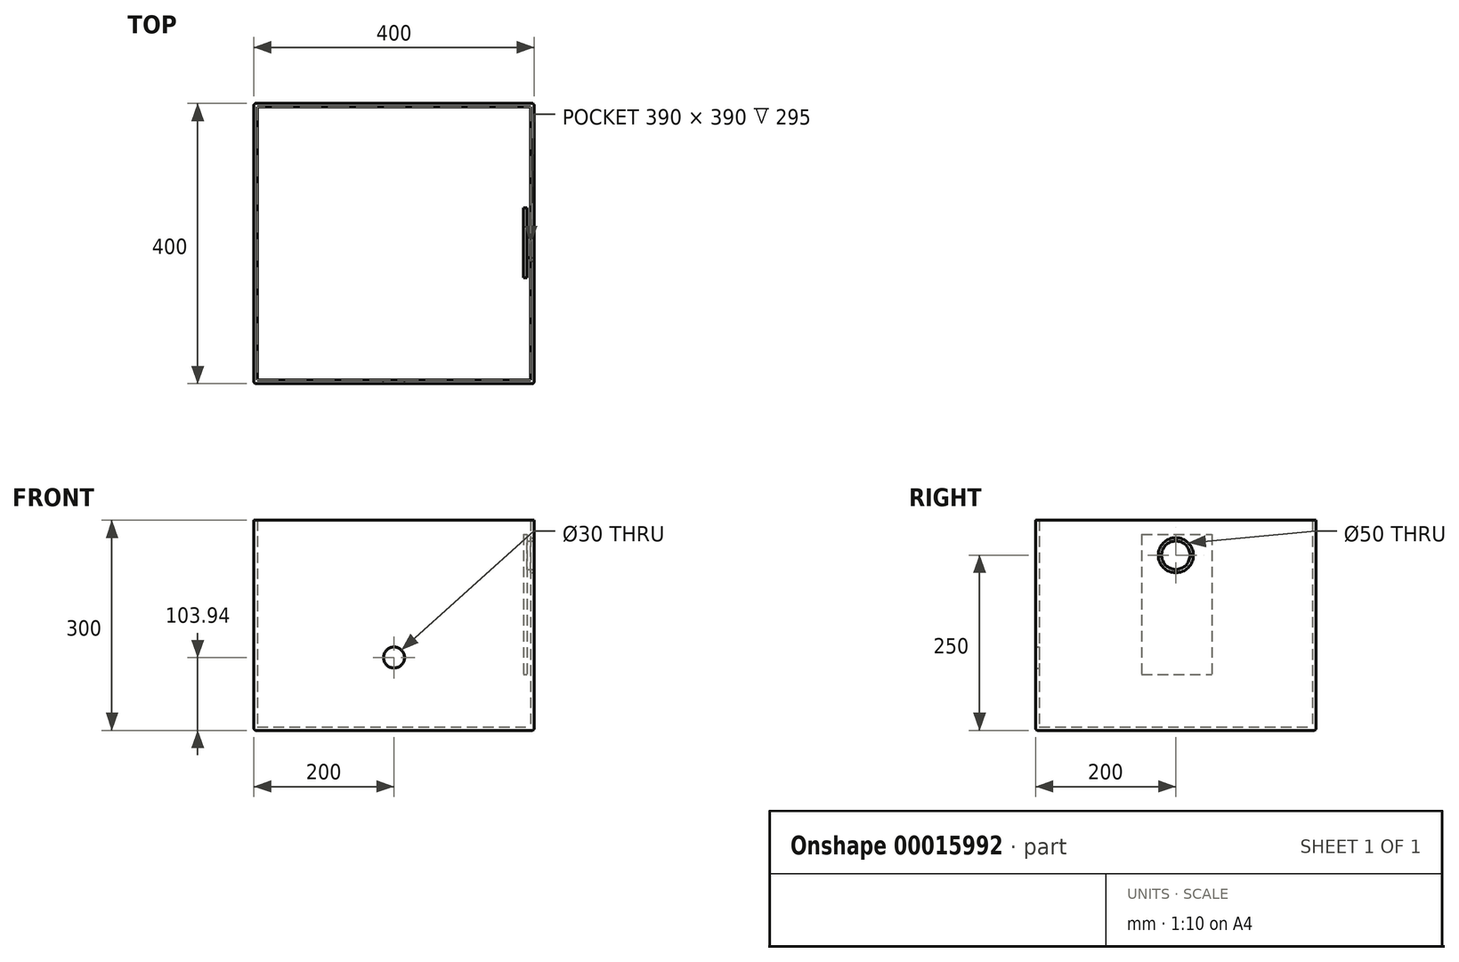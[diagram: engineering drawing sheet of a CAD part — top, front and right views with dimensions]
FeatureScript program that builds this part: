
annotation { "Feature Type Name" : "Feature", "Feature Type Description" : "" }
export const myFeature = defineFeature(function(context is Context, id is Id, definition is map)
    precondition{}
    {
        {
            var Q0;
            Q0=qCreatedBy(makeId("Front.planeOp"),FACE);
            var sketch = newSketch(context, id + "F0", { "sketchPlane" : qUnion([Q0])});
            skLineSegment(sketch, "E0", {"start": v(0, 0) * mm, "end": v(200, 0) * mm});
            skLineSegment(sketch, "E1", {"start": v(200, 0) * mm, "end": v(200, 300) * mm});
            skLineSegment(sketch, "E2", {"start": v(200, 300) * mm, "end": v(195, 300) * mm});
            skLineSegment(sketch, "E3", {"start": v(195, 300) * mm, "end": v(195, 5) * mm});
            skLineSegment(sketch, "E4", {"start": v(195, 5) * mm, "end": v(0, 5) * mm});
            skLineSegment(sketch, "E5", {"start": v(0, 5) * mm, "end": v(0, 0) * mm});
            skLineSegment(sketch, "E6.MirrorCS", {"start": v(-195, 300) * mm, "end": v(-195, 5) * mm});
            skLineSegment(sketch, "E7.MirrorCS", {"start": v(-200, 0) * mm, "end": v(-200, 300) * mm});
            skLineSegment(sketch, "E8.MirrorCS", {"start": v(-200, 300) * mm, "end": v(-195, 300) * mm});
            skLineSegment(sketch, "E9.MirrorCS", {"start": v(-195, 5) * mm, "end": v(0, 5) * mm});
            skLineSegment(sketch, "E10.MirrorCS", {"start": v(0, 0) * mm, "end": v(-200, 0) * mm});
            skSolve(sketch);
        }
        {
            var Q0;
            Q0 = qSketchRegion(id + "F0", true);
            extrude(context, id + "F1", {"entities" : qUnion([Q0]), "depth" : 200 * mm});
        }
        {
            var Q0;
            Q0=makeQuery(id+"F1.opExtrude","SWEPT_FACE",FACE,{"disambiguationData":[OSD([sQuery(id+"F0.wireOp",EDGE,"E4"),sQuery(id+"F0.wireOp",EDGE,"E9.MirrorCS")])]});
            var sketch = newSketch(context, id + "F2", { "sketchPlane" : qUnion([Q0])});
            skLineSegment(sketch, "E11.bottom", {"start": v(-195, -200) * mm, "end": v(195, -200) * mm});
            skLineSegment(sketch, "E11.top", {"start": v(-195, -195) * mm, "end": v(195, -195) * mm});
            skLineSegment(sketch, "E11.left", {"start": v(-195, -200) * mm, "end": v(-195, -195) * mm});
            skLineSegment(sketch, "E11.right", {"start": v(195, -200) * mm, "end": v(195, -195) * mm});
            skSolve(sketch);
        }
        {
            var Q0;
            Q0 = qSketchRegion(id + "F2", true);
            extrude(context, id + "F3", {"entities" : qUnion([Q0]), "operationType" : NewBodyOperationType.ADD, "depth" : 295 * mm});
        }
        {
            var Q0;
            Q0=makeQuery(id+"F1.opExtrude","SWEPT_BODY",BODY,{"disambiguationData":[OSD([sQuery(id+"F0.wireOp",EDGE,"E0"),sQuery(id+"F0.wireOp",EDGE,"E1"),sQuery(id+"F0.wireOp",EDGE,"E2"),sQuery(id+"F0.wireOp",EDGE,"E3"),sQuery(id+"F0.wireOp",EDGE,"E4"),sQuery(id+"F0.wireOp",EDGE,"E6.MirrorCS"),sQuery(id+"F0.wireOp",EDGE,"E7.MirrorCS"),sQuery(id+"F0.wireOp",EDGE,"E8.MirrorCS"),sQuery(id+"F0.wireOp",EDGE,"E9.MirrorCS"),sQuery(id+"F0.wireOp",EDGE,"E10.MirrorCS")])]});
            var Q1;
            Q1=qCreatedBy(makeId("Front.planeOp"),FACE);
            mirror(context, id + "F4", {"operationType" : NewBodyOperationType.ADD, "entities" : qUnion([Q0]), "mirrorPlane" : qUnion([Q1])});
        }
        {
            var Q0;
            {var subQ0=makeQuery(id+"F1.opExtrude","SWEPT_FACE",FACE,{"disambiguationData":[OSD([sQuery(id+"F0.wireOp",EDGE,"E7.MirrorCS")])]});Q0=makeQuery(id+"F4.boolean.opBoolean","MERGE",FACE,{"derivedFrom":[subQ0,makeQuery(id+"F4.opPattern","COPY",FACE,{"derivedFrom":subQ0,"instanceName":"1"})]});}
            var sketch = newSketch(context, id + "F5", { "sketchPlane" : qUnion([Q0])});
            skLineSegment(sketch, "E12.bottom", {"start": v(-200, 300) * mm, "end": v(200, 300) * mm});
            skLineSegment(sketch, "E12.top", {"start": v(-200, 320) * mm, "end": v(200, 320) * mm});
            skLineSegment(sketch, "E12.left", {"start": v(-200, 300) * mm, "end": v(-200, 320) * mm});
            skLineSegment(sketch, "E12.right", {"start": v(200, 300) * mm, "end": v(200, 320) * mm});
            skSolve(sketch);
        }
        {
            var Q0;
            Q0=makeQuery(id+"F4.opPattern","COPY",EDGE,{"derivedFrom":makeQuery(id+"F1.opExtrude","CAP_EDGE",EDGE,{"disambiguationData":[OSD([sQuery(id+"F0.wireOp",EDGE,"E1")])],"isStart":false}),"instanceName":"1"});
            var Q1;
            {var subQ0=makeQuery(id+"F1.opExtrude","SWEPT_EDGE",EDGE,{"disambiguationData":[OSD([sQuery(id+"F0.wireOp",EDGE,"E0"),sQuery(id+"F0.wireOp",EDGE,"E1")])]});Q1=makeQuery(id+"F4.boolean.opBoolean","MERGE",EDGE,{"derivedFrom":[subQ0,makeQuery(id+"F4.opPattern","COPY",EDGE,{"derivedFrom":subQ0,"instanceName":"1"})]});}
            var Q2;
            Q2=makeQuery(id+"F4.opPattern","COPY",EDGE,{"derivedFrom":makeQuery(id+"F1.opExtrude","CAP_EDGE",EDGE,{"disambiguationData":[OSD([sQuery(id+"F0.wireOp",EDGE,"E0"),sQuery(id+"F0.wireOp",EDGE,"E10.MirrorCS")])],"isStart":false}),"instanceName":"1"});
            var Q3;
            Q3=makeQuery(id+"F4.opPattern","COPY",EDGE,{"derivedFrom":makeQuery(id+"F1.opExtrude","CAP_EDGE",EDGE,{"disambiguationData":[OSD([sQuery(id+"F0.wireOp",EDGE,"E7.MirrorCS")])],"isStart":false}),"instanceName":"1"});
            var Q4;
            Q4=makeQuery(id+"F0aFheVfIjX7SRM_1.opExtrude","CAP_EDGE",EDGE,{"disambiguationData":[OSD([sQuery(id+"F5.wireOp",EDGE,"E12.left")])],"isStart":true});
            var Q5;
            Q5=makeQuery(id+"F0aFheVfIjX7SRM_1.opExtrude","CAP_EDGE",EDGE,{"disambiguationData":[OSD([sQuery(id+"F5.wireOp",EDGE,"E12.left")])],"isStart":false});
            var Q6;
            Q6=makeQuery(id+"F1.opExtrude","CAP_EDGE",EDGE,{"disambiguationData":[OSD([sQuery(id+"F0.wireOp",EDGE,"E1")])],"isStart":false});
            var Q7;
            Q7=makeQuery(id+"F0aFheVfIjX7SRM_1.opExtrude","CAP_EDGE",EDGE,{"disambiguationData":[OSD([sQuery(id+"F5.wireOp",EDGE,"E12.right")])],"isStart":false});
            var Q8;
            Q8=makeQuery(id+"F1.opExtrude","CAP_EDGE",EDGE,{"disambiguationData":[OSD([sQuery(id+"F0.wireOp",EDGE,"E7.MirrorCS")])],"isStart":false});
            var Q9;
            {var subQ0=makeQuery(id+"F1.opExtrude","SWEPT_EDGE",EDGE,{"disambiguationData":[OSD([sQuery(id+"F0.wireOp",EDGE,"E7.MirrorCS"),sQuery(id+"F0.wireOp",EDGE,"E10.MirrorCS")])]});Q9=makeQuery(id+"F4.boolean.opBoolean","MERGE",EDGE,{"derivedFrom":[subQ0,makeQuery(id+"F4.opPattern","COPY",EDGE,{"derivedFrom":subQ0,"instanceName":"1"})]});}
            var Q10;
            Q10=makeQuery(id+"F1.opExtrude","CAP_EDGE",EDGE,{"disambiguationData":[OSD([sQuery(id+"F0.wireOp",EDGE,"E0"),sQuery(id+"F0.wireOp",EDGE,"E10.MirrorCS")])],"isStart":false});
            var Q11;
            Q11=makeQuery(id+"F0aFheVfIjX7SRM_1.opExtrude","CAP_EDGE",EDGE,{"disambiguationData":[OSD([sQuery(id+"F5.wireOp",EDGE,"E12.right")])],"isStart":true});
            var Q12;
            Q12=makeQuery(id+"F0aFheVfIjX7SRM_1.opExtrude","SWEPT_FACE",FACE,{"disambiguationData":[OSD([sQuery(id+"F5.wireOp",EDGE,"E12.top")])]});
            fillet(context, id + "F6", {"entities" : qUnion([Q0, Q1, Q2, Q3, Q4, Q5, Q6, Q7, Q8, Q9, Q10, Q11, Q12]), "radius" : 3 * mm, "tangentPropagation" : true, "allowEdgeOverflow" : false});
        }
        {
            var Q0;
            Q0=makeQuery(id+"F3.opExtrude","SWEPT_FACE",FACE,{"disambiguationData":[OSD([sQuery(id+"F2.wireOp",EDGE,"E11.top")])]});
            var sketch = newSketch(context, id + "F7", { "sketchPlane" : qUnion([Q0])});
            skCircle(sketch, "E13", {"center": v(0, 103.94) * mm, "radius": 15 * mm});
            skSolve(sketch);
        }
        {
            var Q0;
            Q0 = qSketchRegion(id + "F7", true);
            var Q1;
            Q1=makeQuery(id+"F3.boolean.opBoolean","MERGE",FACE,{"derivedFrom":[makeQuery(id+"F1.opExtrude","CAP_FACE",FACE,{"disambiguationData":[OSD([sQuery(id+"F0.wireOp",EDGE,"E0"),sQuery(id+"F0.wireOp",EDGE,"E1"),sQuery(id+"F0.wireOp",EDGE,"E2"),sQuery(id+"F0.wireOp",EDGE,"E3"),sQuery(id+"F0.wireOp",EDGE,"E4"),sQuery(id+"F0.wireOp",EDGE,"E6.MirrorCS"),sQuery(id+"F0.wireOp",EDGE,"E7.MirrorCS"),sQuery(id+"F0.wireOp",EDGE,"E8.MirrorCS"),sQuery(id+"F0.wireOp",EDGE,"E9.MirrorCS"),sQuery(id+"F0.wireOp",EDGE,"E10.MirrorCS")])],"isStart":false}),makeQuery(id+"F3.opExtrude","SWEPT_FACE",FACE,{"disambiguationData":[OSD([sQuery(id+"F2.wireOp",EDGE,"E11.bottom")])]})]});
            extrude(context, id + "F8", {"entities" : qUnion([Q0]), "operationType" : NewBodyOperationType.REMOVE, "endBound" : BoundingType.UP_TO_SURFACE, "oppositeDirection" : true, "endBoundEntityFace" : qUnion([Q1]), "depth" : 25.4 * mm});
        }
        {
            var Q0;
            {var subQ0=makeQuery(id+"F1.opExtrude","SWEPT_FACE",FACE,{"disambiguationData":[OSD([sQuery(id+"F0.wireOp",EDGE,"E1")])]});Q0=makeQuery(id+"F4.boolean.opBoolean","MERGE",FACE,{"derivedFrom":[subQ0,makeQuery(id+"F4.opPattern","COPY",FACE,{"derivedFrom":subQ0,"instanceName":"1"})]});}
            var sketch = newSketch(context, id + "F9", { "sketchPlane" : qUnion([Q0])});
            skCircle(sketch, "E14", {"center": v(0, 250) * mm, "radius": 25 * mm});
            skSolve(sketch);
        }
        {
            var Q0;
            Q0 = qSketchRegion(id + "F9", true);
            extrude(context, id + "F10", {"entities" : qUnion([Q0]), "operationType" : NewBodyOperationType.REMOVE, "oppositeDirection" : true, "depth" : 25.4 * mm});
        }
        {
            var Q0;
            {var subQ0=makeQuery(id+"F1.opExtrude","SWEPT_FACE",FACE,{"disambiguationData":[OSD([sQuery(id+"F0.wireOp",EDGE,"E1")])]});Q0=makeQuery(id+"F4.boolean.opBoolean","MERGE",FACE,{"derivedFrom":[subQ0,makeQuery(id+"F4.opPattern","COPY",FACE,{"derivedFrom":subQ0,"instanceName":"1"})]});}
            var sketch = newSketch(context, id + "F11", { "sketchPlane" : qUnion([Q0])});
            skCircle(sketch, "E15", {"center": v(0, 250) * mm, "radius": 20.29 * mm});
            skSolve(sketch);
        }
        {
            var Q0;
            Q0 = qSketchRegion(id + "F11", true);
            extrude(context, id + "F12", {"entities" : qUnion([Q0]), "oppositeDirection" : true, "depth" : 10 * mm});
        }
        {
            var Q0;
            Q0=makeQuery(id+"F12.opExtrude","CAP_FACE",FACE,{"disambiguationData":[OSD([sQuery(id+"F11.wireOp",EDGE,"E15")])],"isStart":false});
            var sketch = newSketch(context, id + "F13", { "sketchPlane" : qUnion([Q0])});
            skLineSegment(sketch, "E16.bottom", {"start": v(48.84, 279.71) * mm, "end": v(-51.16, 279.71) * mm});
            skLineSegment(sketch, "E16.top", {"start": v(48.84, 79.71) * mm, "end": v(-51.16, 79.71) * mm});
            skLineSegment(sketch, "E16.left", {"start": v(48.84, 279.71) * mm, "end": v(48.84, 79.71) * mm});
            skLineSegment(sketch, "E16.right", {"start": v(-51.16, 279.71) * mm, "end": v(-51.16, 79.71) * mm});
            skSolve(sketch);
        }
        {
            var Q0;
            Q0 = qSketchRegion(id + "F13", true);
            extrude(context, id + "F14", {"entities" : qUnion([Q0]), "operationType" : NewBodyOperationType.ADD, "depth" : 5 * mm});
        }
        {
            var Q0;
            Q0=makeQuery(id+"F14.opExtrude","SWEPT_FACE",FACE,{"disambiguationData":[OSD([sQuery(id+"F13.wireOp",EDGE,"E16.bottom")])]});
            var sketch = newSketch(context, id + "F15", { "sketchPlane" : qUnion([Q0])});
            skLineSegment(sketch, "E17", {"start": v(185, 51.16) * mm, "end": v(170, 51.16) * mm});
            skLineSegment(sketch, "E18", {"start": v(170, 51.16) * mm, "end": v(170, 50.16) * mm});
            skLineSegment(sketch, "E19", {"start": v(170, 50.16) * mm, "end": v(180, 50.16) * mm});
            skLineSegment(sketch, "E20", {"start": v(180, 50.16) * mm, "end": v(180, 48.16) * mm});
            skLineSegment(sketch, "E21", {"start": v(180, 48.16) * mm, "end": v(170, 48.16) * mm});
            skLineSegment(sketch, "E22.1.0.0", {"start": v(170, 48.16) * mm, "end": v(170, 47.16) * mm});
            skLineSegment(sketch, "E22.1.0.1", {"start": v(170, 47.16) * mm, "end": v(180, 47.16) * mm});
            skLineSegment(sketch, "E22.1.0.2", {"start": v(180, 47.16) * mm, "end": v(180, 45.16) * mm});
            skLineSegment(sketch, "E22.1.0.3", {"start": v(180, 45.16) * mm, "end": v(170, 45.16) * mm});
            skLineSegment(sketch, "E22.2.0.0", {"start": v(169.99, 45.16) * mm, "end": v(169.99, 44.16) * mm});
            skLineSegment(sketch, "E22.2.0.1", {"start": v(169.99, 44.16) * mm, "end": v(179.99, 44.16) * mm});
            skLineSegment(sketch, "E22.2.0.2", {"start": v(179.99, 44.16) * mm, "end": v(179.99, 42.16) * mm});
            skLineSegment(sketch, "E22.2.0.3", {"start": v(179.99, 42.16) * mm, "end": v(169.99, 42.16) * mm});
            skLineSegment(sketch, "E22.3.0.0", {"start": v(169.98, 42.16) * mm, "end": v(169.98, 41.16) * mm});
            skLineSegment(sketch, "E22.3.0.1", {"start": v(169.98, 41.16) * mm, "end": v(179.98, 41.16) * mm});
            skLineSegment(sketch, "E22.3.0.2", {"start": v(179.98, 41.16) * mm, "end": v(179.98, 39.16) * mm});
            skLineSegment(sketch, "E22.3.0.3", {"start": v(179.98, 39.16) * mm, "end": v(169.98, 39.16) * mm});
            skLineSegment(sketch, "E22.4.0.0", {"start": v(169.97, 39.16) * mm, "end": v(169.97, 38.16) * mm});
            skLineSegment(sketch, "E22.4.0.1", {"start": v(169.97, 38.16) * mm, "end": v(179.97, 38.16) * mm});
            skLineSegment(sketch, "E22.4.0.2", {"start": v(179.97, 38.16) * mm, "end": v(179.97, 36.16) * mm});
            skLineSegment(sketch, "E22.4.0.3", {"start": v(179.97, 36.16) * mm, "end": v(169.97, 36.16) * mm});
            skLineSegment(sketch, "E22.5.0.0", {"start": v(169.97, 36.16) * mm, "end": v(169.97, 35.16) * mm});
            skLineSegment(sketch, "E22.5.0.1", {"start": v(169.97, 35.16) * mm, "end": v(179.97, 35.16) * mm});
            skLineSegment(sketch, "E22.5.0.2", {"start": v(179.97, 35.16) * mm, "end": v(179.97, 33.16) * mm});
            skLineSegment(sketch, "E22.5.0.3", {"start": v(179.97, 33.16) * mm, "end": v(169.97, 33.16) * mm});
            skLineSegment(sketch, "E22.6.0.0", {"start": v(169.96, 33.16) * mm, "end": v(169.96, 32.16) * mm});
            skLineSegment(sketch, "E22.6.0.1", {"start": v(169.96, 32.16) * mm, "end": v(179.96, 32.16) * mm});
            skLineSegment(sketch, "E22.6.0.2", {"start": v(179.96, 32.16) * mm, "end": v(179.96, 30.16) * mm});
            skLineSegment(sketch, "E22.6.0.3", {"start": v(179.96, 30.16) * mm, "end": v(169.96, 30.16) * mm});
            skLineSegment(sketch, "E22.7.0.0", {"start": v(169.95, 30.16) * mm, "end": v(169.95, 29.16) * mm});
            skLineSegment(sketch, "E22.7.0.1", {"start": v(169.95, 29.16) * mm, "end": v(179.95, 29.16) * mm});
            skLineSegment(sketch, "E22.7.0.2", {"start": v(179.95, 29.16) * mm, "end": v(179.95, 27.16) * mm});
            skLineSegment(sketch, "E22.7.0.3", {"start": v(179.95, 27.16) * mm, "end": v(169.95, 27.16) * mm});
            skLineSegment(sketch, "E22.8.0.0", {"start": v(169.95, 27.16) * mm, "end": v(169.95, 26.16) * mm});
            skLineSegment(sketch, "E22.8.0.1", {"start": v(169.95, 26.16) * mm, "end": v(179.95, 26.16) * mm});
            skLineSegment(sketch, "E22.8.0.2", {"start": v(179.95, 26.16) * mm, "end": v(179.95, 24.16) * mm});
            skLineSegment(sketch, "E22.8.0.3", {"start": v(179.95, 24.16) * mm, "end": v(169.95, 24.16) * mm});
            skLineSegment(sketch, "E22.9.0.0", {"start": v(169.94, 24.16) * mm, "end": v(169.94, 23.16) * mm});
            skLineSegment(sketch, "E22.9.0.1", {"start": v(169.94, 23.16) * mm, "end": v(179.94, 23.16) * mm});
            skLineSegment(sketch, "E22.9.0.2", {"start": v(179.94, 23.16) * mm, "end": v(179.94, 21.16) * mm});
            skLineSegment(sketch, "E22.9.0.3", {"start": v(179.94, 21.16) * mm, "end": v(169.94, 21.16) * mm});
            skLineSegment(sketch, "E22.10.0.0", {"start": v(169.93, 21.16) * mm, "end": v(169.93, 20.16) * mm});
            skLineSegment(sketch, "E22.10.0.1", {"start": v(169.93, 20.16) * mm, "end": v(179.93, 20.16) * mm});
            skLineSegment(sketch, "E22.10.0.2", {"start": v(179.93, 20.16) * mm, "end": v(179.93, 18.16) * mm});
            skLineSegment(sketch, "E22.10.0.3", {"start": v(179.93, 18.16) * mm, "end": v(169.93, 18.16) * mm});
            skLineSegment(sketch, "E22.11.0.0", {"start": v(169.93, 18.16) * mm, "end": v(169.93, 17.16) * mm});
            skLineSegment(sketch, "E22.11.0.1", {"start": v(169.93, 17.16) * mm, "end": v(179.93, 17.16) * mm});
            skLineSegment(sketch, "E22.11.0.2", {"start": v(179.93, 17.16) * mm, "end": v(179.93, 15.16) * mm});
            skLineSegment(sketch, "E22.11.0.3", {"start": v(179.93, 15.16) * mm, "end": v(169.93, 15.16) * mm});
            skLineSegment(sketch, "E22.12.0.0", {"start": v(169.92, 15.16) * mm, "end": v(169.92, 14.16) * mm});
            skLineSegment(sketch, "E22.12.0.1", {"start": v(169.92, 14.16) * mm, "end": v(179.92, 14.16) * mm});
            skLineSegment(sketch, "E22.12.0.2", {"start": v(179.92, 14.16) * mm, "end": v(179.92, 12.16) * mm});
            skLineSegment(sketch, "E22.12.0.3", {"start": v(179.92, 12.16) * mm, "end": v(169.92, 12.16) * mm});
            skLineSegment(sketch, "E22.13.0.0", {"start": v(169.91, 12.16) * mm, "end": v(169.91, 11.16) * mm});
            skLineSegment(sketch, "E22.13.0.1", {"start": v(169.91, 11.16) * mm, "end": v(179.91, 11.16) * mm});
            skLineSegment(sketch, "E22.13.0.2", {"start": v(179.91, 11.16) * mm, "end": v(179.91, 9.16) * mm});
            skLineSegment(sketch, "E22.13.0.3", {"start": v(179.91, 9.16) * mm, "end": v(169.91, 9.16) * mm});
            skLineSegment(sketch, "E22.14.0.0", {"start": v(169.9, 9.16) * mm, "end": v(169.9, 8.16) * mm});
            skLineSegment(sketch, "E22.14.0.1", {"start": v(169.9, 8.16) * mm, "end": v(179.9, 8.16) * mm});
            skLineSegment(sketch, "E22.14.0.2", {"start": v(179.9, 8.16) * mm, "end": v(179.9, 6.16) * mm});
            skLineSegment(sketch, "E22.14.0.3", {"start": v(179.9, 6.16) * mm, "end": v(169.9, 6.16) * mm});
            skLineSegment(sketch, "E22.15.0.0", {"start": v(169.9, 6.16) * mm, "end": v(169.9, 5.16) * mm});
            skLineSegment(sketch, "E22.15.0.1", {"start": v(169.9, 5.16) * mm, "end": v(179.9, 5.16) * mm});
            skLineSegment(sketch, "E22.15.0.2", {"start": v(179.9, 5.16) * mm, "end": v(179.9, 3.16) * mm});
            skLineSegment(sketch, "E22.15.0.3", {"start": v(179.9, 3.16) * mm, "end": v(169.9, 3.16) * mm});
            skLineSegment(sketch, "E22.16.0.0", {"start": v(169.9, 3.16) * mm, "end": v(169.9, 2.16) * mm});
            skLineSegment(sketch, "E22.16.0.1", {"start": v(169.9, 2.16) * mm, "end": v(179.9, 2.16) * mm});
            skLineSegment(sketch, "E22.16.0.2", {"start": v(179.9, 2.16) * mm, "end": v(179.9, 0.16) * mm});
            skLineSegment(sketch, "E22.16.0.3", {"start": v(179.9, 0.16) * mm, "end": v(169.9, 0.16) * mm});
            skLineSegment(sketch, "E22.17.0.0", {"start": v(169.89, 0.16) * mm, "end": v(169.89, -0.84) * mm});
            skLineSegment(sketch, "E22.17.0.1", {"start": v(169.89, -0.84) * mm, "end": v(179.89, -0.84) * mm});
            skLineSegment(sketch, "E22.17.0.2", {"start": v(179.89, -0.84) * mm, "end": v(179.89, -2.84) * mm});
            skLineSegment(sketch, "E22.17.0.3", {"start": v(179.89, -2.84) * mm, "end": v(169.89, -2.84) * mm});
            skLineSegment(sketch, "E22.18.0.0", {"start": v(169.88, -2.84) * mm, "end": v(169.88, -3.84) * mm});
            skLineSegment(sketch, "E22.18.0.1", {"start": v(169.88, -3.84) * mm, "end": v(179.88, -3.84) * mm});
            skLineSegment(sketch, "E22.18.0.2", {"start": v(179.88, -3.84) * mm, "end": v(179.88, -5.84) * mm});
            skLineSegment(sketch, "E22.18.0.3", {"start": v(179.88, -5.84) * mm, "end": v(169.88, -5.84) * mm});
            skLineSegment(sketch, "E22.19.0.0", {"start": v(169.87, -5.84) * mm, "end": v(169.87, -6.84) * mm});
            skLineSegment(sketch, "E22.19.0.1", {"start": v(169.87, -6.84) * mm, "end": v(179.87, -6.84) * mm});
            skLineSegment(sketch, "E22.19.0.2", {"start": v(179.87, -6.84) * mm, "end": v(179.87, -8.84) * mm});
            skLineSegment(sketch, "E22.19.0.3", {"start": v(179.87, -8.84) * mm, "end": v(169.87, -8.84) * mm});
            skLineSegment(sketch, "E22.20.0.0", {"start": v(169.87, -8.84) * mm, "end": v(169.87, -9.84) * mm});
            skLineSegment(sketch, "E22.20.0.1", {"start": v(169.87, -9.84) * mm, "end": v(179.87, -9.84) * mm});
            skLineSegment(sketch, "E22.20.0.2", {"start": v(179.87, -9.84) * mm, "end": v(179.87, -11.84) * mm});
            skLineSegment(sketch, "E22.20.0.3", {"start": v(179.87, -11.84) * mm, "end": v(169.87, -11.84) * mm});
            skLineSegment(sketch, "E22.21.0.0", {"start": v(169.86, -11.84) * mm, "end": v(169.86, -12.84) * mm});
            skLineSegment(sketch, "E22.21.0.1", {"start": v(169.86, -12.84) * mm, "end": v(179.86, -12.84) * mm});
            skLineSegment(sketch, "E22.21.0.2", {"start": v(179.86, -12.84) * mm, "end": v(179.86, -14.84) * mm});
            skLineSegment(sketch, "E22.21.0.3", {"start": v(179.86, -14.84) * mm, "end": v(169.86, -14.84) * mm});
            skLineSegment(sketch, "E22.22.0.0", {"start": v(169.85, -14.84) * mm, "end": v(169.85, -15.84) * mm});
            skLineSegment(sketch, "E22.22.0.1", {"start": v(169.85, -15.84) * mm, "end": v(179.85, -15.84) * mm});
            skLineSegment(sketch, "E22.22.0.2", {"start": v(179.85, -15.84) * mm, "end": v(179.85, -17.84) * mm});
            skLineSegment(sketch, "E22.22.0.3", {"start": v(179.85, -17.84) * mm, "end": v(169.85, -17.84) * mm});
            skLineSegment(sketch, "E22.23.0.0", {"start": v(169.85, -17.84) * mm, "end": v(169.85, -18.84) * mm});
            skLineSegment(sketch, "E22.23.0.1", {"start": v(169.85, -18.84) * mm, "end": v(179.85, -18.84) * mm});
            skLineSegment(sketch, "E22.23.0.2", {"start": v(179.85, -18.84) * mm, "end": v(179.85, -20.84) * mm});
            skLineSegment(sketch, "E22.23.0.3", {"start": v(179.85, -20.84) * mm, "end": v(169.85, -20.84) * mm});
            skLineSegment(sketch, "E22.24.0.0", {"start": v(169.84, -20.84) * mm, "end": v(169.84, -21.84) * mm});
            skLineSegment(sketch, "E22.24.0.1", {"start": v(169.84, -21.84) * mm, "end": v(179.84, -21.84) * mm});
            skLineSegment(sketch, "E22.24.0.2", {"start": v(179.84, -21.84) * mm, "end": v(179.84, -23.84) * mm});
            skLineSegment(sketch, "E22.24.0.3", {"start": v(179.84, -23.84) * mm, "end": v(169.84, -23.84) * mm});
            skLineSegment(sketch, "E22.25.0.0", {"start": v(169.83, -23.84) * mm, "end": v(169.83, -24.84) * mm});
            skLineSegment(sketch, "E22.25.0.1", {"start": v(169.83, -24.84) * mm, "end": v(179.83, -24.84) * mm});
            skLineSegment(sketch, "E22.25.0.2", {"start": v(179.83, -24.84) * mm, "end": v(179.83, -26.84) * mm});
            skLineSegment(sketch, "E22.25.0.3", {"start": v(179.83, -26.84) * mm, "end": v(169.83, -26.84) * mm});
            skLineSegment(sketch, "E22.26.0.0", {"start": v(169.83, -26.84) * mm, "end": v(169.83, -27.84) * mm});
            skLineSegment(sketch, "E22.26.0.1", {"start": v(169.83, -27.84) * mm, "end": v(179.83, -27.84) * mm});
            skLineSegment(sketch, "E22.26.0.2", {"start": v(179.83, -27.84) * mm, "end": v(179.83, -29.84) * mm});
            skLineSegment(sketch, "E22.26.0.3", {"start": v(179.83, -29.84) * mm, "end": v(169.83, -29.84) * mm});
            skLineSegment(sketch, "E22.27.0.0", {"start": v(169.82, -29.84) * mm, "end": v(169.82, -30.84) * mm});
            skLineSegment(sketch, "E22.27.0.1", {"start": v(169.82, -30.84) * mm, "end": v(179.82, -30.84) * mm});
            skLineSegment(sketch, "E22.27.0.2", {"start": v(179.82, -30.84) * mm, "end": v(179.82, -32.84) * mm});
            skLineSegment(sketch, "E22.27.0.3", {"start": v(179.82, -32.84) * mm, "end": v(169.82, -32.84) * mm});
            skLineSegment(sketch, "E22.28.0.0", {"start": v(169.81, -32.84) * mm, "end": v(169.81, -33.84) * mm});
            skLineSegment(sketch, "E22.28.0.1", {"start": v(169.81, -33.84) * mm, "end": v(179.81, -33.84) * mm});
            skLineSegment(sketch, "E22.28.0.2", {"start": v(179.81, -33.84) * mm, "end": v(179.81, -35.84) * mm});
            skLineSegment(sketch, "E22.28.0.3", {"start": v(179.81, -35.84) * mm, "end": v(169.81, -35.84) * mm});
            skLineSegment(sketch, "E22.29.0.0", {"start": v(169.8, -35.84) * mm, "end": v(169.8, -36.84) * mm});
            skLineSegment(sketch, "E22.29.0.1", {"start": v(169.8, -36.84) * mm, "end": v(179.8, -36.84) * mm});
            skLineSegment(sketch, "E22.29.0.2", {"start": v(179.8, -36.84) * mm, "end": v(179.8, -38.84) * mm});
            skLineSegment(sketch, "E22.29.0.3", {"start": v(179.8, -38.84) * mm, "end": v(169.8, -38.84) * mm});
            skLineSegment(sketch, "E22.30.0.0", {"start": v(169.8, -38.84) * mm, "end": v(169.8, -39.84) * mm});
            skLineSegment(sketch, "E22.30.0.1", {"start": v(169.8, -39.84) * mm, "end": v(179.8, -39.84) * mm});
            skLineSegment(sketch, "E22.30.0.2", {"start": v(179.8, -39.84) * mm, "end": v(179.8, -41.84) * mm});
            skLineSegment(sketch, "E22.30.0.3", {"start": v(179.8, -41.84) * mm, "end": v(169.8, -41.84) * mm});
            skLineSegment(sketch, "E22.31.0.0", {"start": v(169.8, -41.84) * mm, "end": v(169.8, -42.84) * mm});
            skLineSegment(sketch, "E22.31.0.1", {"start": v(169.8, -42.84) * mm, "end": v(179.8, -42.84) * mm});
            skLineSegment(sketch, "E22.31.0.2", {"start": v(179.8, -42.84) * mm, "end": v(179.8, -44.84) * mm});
            skLineSegment(sketch, "E22.31.0.3", {"start": v(179.8, -44.84) * mm, "end": v(169.8, -44.84) * mm});
            skLineSegment(sketch, "E22.32.0.0", {"start": v(169.79, -44.84) * mm, "end": v(169.79, -45.84) * mm});
            skLineSegment(sketch, "E22.32.0.1", {"start": v(169.79, -45.84) * mm, "end": v(179.79, -45.84) * mm});
            skLineSegment(sketch, "E22.32.0.2", {"start": v(179.79, -45.84) * mm, "end": v(179.79, -47.84) * mm});
            skLineSegment(sketch, "E22.32.0.3", {"start": v(179.79, -47.84) * mm, "end": v(169.79, -47.84) * mm});
            skLineSegment(sketch, "E22.33.0.0", {"start": v(169.78, -47.84) * mm, "end": v(169.78, -48.84) * mm});
            skLineSegment(sketch, "E22.33.0.1", {"start": v(169.78, -48.84) * mm, "end": v(185, -48.84) * mm});
            skLineSegment(sketch, "E23", {"start": v(185, 51.16) * mm, "end": v(185, -48.84) * mm});
            skSolve(sketch);
        }
        {
            var Q0;
            Q0=sQuery(id+"F15.wireOp",EDGE,"E22.18.0.3");
            var Q1;
            Q1=sQuery(id+"F15.wireOp",EDGE,"E22.14.0.3");
            var Q2;
            Q2=sQuery(id+"F15.wireOp",EDGE,"E22.10.0.3");
            var Q3;
            Q3=sQuery(id+"F15.wireOp",EDGE,"E22.6.0.3");
            var Q4;
            Q4=sQuery(id+"F15.wireOp",EDGE,"E22.30.0.3");
            var Q5;
            Q5=sQuery(id+"F15.wireOp",EDGE,"E22.26.0.3");
            var Q6;
            Q6=sQuery(id+"F15.wireOp",EDGE,"E22.22.0.3");
            var Q7;
            Q7=sQuery(id+"F15.wireOp",EDGE,"E22.3.0.1");
            var Q8;
            Q8=sQuery(id+"F15.wireOp",EDGE,"E19");
            var Q9;
            Q9=sQuery(id+"F15.wireOp",EDGE,"E21");
            var Q10;
            Q10=sQuery(id+"F15.wireOp",EDGE,"E22.1.0.1");
            var Q11;
            Q11=sQuery(id+"F15.wireOp",EDGE,"E22.1.0.3");
            var Q12;
            Q12=sQuery(id+"F15.wireOp",EDGE,"E22.2.0.1");
            var Q13;
            Q13=sQuery(id+"F15.wireOp",EDGE,"E22.2.0.3");
            var Q14;
            Q14=sQuery(id+"F15.wireOp",EDGE,"E22.7.0.1");
            var Q15;
            Q15=sQuery(id+"F15.wireOp",EDGE,"E22.23.0.1");
            var Q16;
            Q16=sQuery(id+"F15.wireOp",EDGE,"E22.19.0.1");
            var Q17;
            Q17=sQuery(id+"F15.wireOp",EDGE,"E22.15.0.1");
            var Q18;
            Q18=sQuery(id+"F15.wireOp",EDGE,"E22.11.0.1");
            var Q19;
            Q19=sQuery(id+"F15.wireOp",EDGE,"E22.31.0.1");
            var Q20;
            Q20=sQuery(id+"F15.wireOp",EDGE,"E22.27.0.1");
            var Q21;
            Q21=sQuery(id+"F15.wireOp",EDGE,"E22.7.0.3");
            var Q22;
            Q22=sQuery(id+"F15.wireOp",EDGE,"E22.3.0.3");
            var Q23;
            Q23=sQuery(id+"F15.wireOp",EDGE,"E22.23.0.3");
            var Q24;
            Q24=sQuery(id+"F15.wireOp",EDGE,"E22.19.0.3");
            var Q25;
            Q25=sQuery(id+"F15.wireOp",EDGE,"E22.15.0.3");
            var Q26;
            Q26=sQuery(id+"F15.wireOp",EDGE,"E22.11.0.3");
            var Q27;
            Q27=sQuery(id+"F15.wireOp",EDGE,"E22.31.0.3");
            var Q28;
            Q28=sQuery(id+"F15.wireOp",EDGE,"E22.27.0.3");
            var Q29;
            Q29=sQuery(id+"F15.wireOp",EDGE,"E22.8.0.1");
            var Q30;
            Q30=sQuery(id+"F15.wireOp",EDGE,"E22.4.0.1");
            var Q31;
            Q31=sQuery(id+"F15.wireOp",EDGE,"E22.24.0.1");
            var Q32;
            Q32=sQuery(id+"F15.wireOp",EDGE,"E22.20.0.1");
            var Q33;
            Q33=sQuery(id+"F15.wireOp",EDGE,"E22.16.0.1");
            var Q34;
            Q34=sQuery(id+"F15.wireOp",EDGE,"E22.12.0.1");
            var Q35;
            Q35=sQuery(id+"F15.wireOp",EDGE,"E22.32.0.1");
            var Q36;
            Q36=sQuery(id+"F15.wireOp",EDGE,"E22.28.0.1");
            var Q37;
            Q37=sQuery(id+"F15.wireOp",EDGE,"E22.8.0.3");
            var Q38;
            Q38=sQuery(id+"F15.wireOp",EDGE,"E22.4.0.3");
            var Q39;
            Q39=sQuery(id+"F15.wireOp",EDGE,"E22.24.0.3");
            var Q40;
            Q40=sQuery(id+"F15.wireOp",EDGE,"E22.20.0.3");
            var Q41;
            Q41=sQuery(id+"F15.wireOp",EDGE,"E22.16.0.3");
            var Q42;
            Q42=sQuery(id+"F15.wireOp",EDGE,"E22.12.0.3");
            var Q43;
            Q43=sQuery(id+"F15.wireOp",EDGE,"E22.32.0.3");
            var Q44;
            Q44=sQuery(id+"F15.wireOp",EDGE,"E22.28.0.3");
            var Q45;
            Q45=sQuery(id+"F15.wireOp",EDGE,"E22.9.0.1");
            var Q46;
            Q46=sQuery(id+"F15.wireOp",EDGE,"E22.5.0.1");
            var Q47;
            Q47=sQuery(id+"F15.wireOp",EDGE,"E22.25.0.1");
            var Q48;
            Q48=sQuery(id+"F15.wireOp",EDGE,"E22.21.0.1");
            var Q49;
            Q49=sQuery(id+"F15.wireOp",EDGE,"E22.17.0.1");
            var Q50;
            Q50=sQuery(id+"F15.wireOp",EDGE,"E22.13.0.1");
            var Q51;
            Q51=sQuery(id+"F15.wireOp",EDGE,"E22.29.0.1");
            var Q52;
            Q52=sQuery(id+"F15.wireOp",EDGE,"E22.17.0.3");
            var Q53;
            Q53=sQuery(id+"F15.wireOp",EDGE,"E22.13.0.3");
            var Q54;
            Q54=sQuery(id+"F15.wireOp",EDGE,"E22.9.0.3");
            var Q55;
            Q55=sQuery(id+"F15.wireOp",EDGE,"E22.5.0.3");
            var Q56;
            Q56=sQuery(id+"F15.wireOp",EDGE,"E22.29.0.3");
            var Q57;
            Q57=sQuery(id+"F15.wireOp",EDGE,"E22.25.0.3");
            var Q58;
            Q58=sQuery(id+"F15.wireOp",EDGE,"E22.21.0.3");
            var Q59;
            Q59=sQuery(id+"F15.wireOp",EDGE,"E22.18.0.1");
            var Q60;
            Q60=sQuery(id+"F15.wireOp",EDGE,"E22.14.0.1");
            var Q61;
            Q61=sQuery(id+"F15.wireOp",EDGE,"E22.10.0.1");
            var Q62;
            Q62=sQuery(id+"F15.wireOp",EDGE,"E22.6.0.1");
            var Q63;
            Q63=sQuery(id+"F15.wireOp",EDGE,"E22.30.0.1");
            var Q64;
            Q64=sQuery(id+"F15.wireOp",EDGE,"E22.26.0.1");
            var Q65;
            Q65=sQuery(id+"F15.wireOp",EDGE,"E22.22.0.1");
            var Q66;
            Q66=sQuery(id+"F15.wireOp",EDGE,"E22.18.0.2");
            var Q67;
            Q67=sQuery(id+"F15.wireOp",EDGE,"E22.14.0.2");
            var Q68;
            Q68=sQuery(id+"F15.wireOp",EDGE,"E22.10.0.2");
            var Q69;
            Q69=sQuery(id+"F15.wireOp",EDGE,"E22.6.0.2");
            var Q70;
            Q70=sQuery(id+"F15.wireOp",EDGE,"E22.30.0.2");
            var Q71;
            Q71=sQuery(id+"F15.wireOp",EDGE,"E22.26.0.2");
            var Q72;
            Q72=sQuery(id+"F15.wireOp",EDGE,"E22.3.0.2");
            var Q73;
            Q73=sQuery(id+"F15.wireOp",EDGE,"E18");
            var Q74;
            Q74=sQuery(id+"F15.wireOp",EDGE,"E20");
            var Q75;
            Q75=sQuery(id+"F15.wireOp",EDGE,"E22.1.0.0");
            var Q76;
            Q76=sQuery(id+"F15.wireOp",EDGE,"E22.1.0.2");
            var Q77;
            Q77=sQuery(id+"F15.wireOp",EDGE,"E22.2.0.0");
            var Q78;
            Q78=sQuery(id+"F15.wireOp",EDGE,"E22.19.0.0");
            var Q79;
            Q79=sQuery(id+"F15.wireOp",EDGE,"E22.7.0.2");
            var Q80;
            Q80=sQuery(id+"F15.wireOp",EDGE,"E22.23.0.2");
            var Q81;
            Q81=sQuery(id+"F15.wireOp",EDGE,"E22.19.0.2");
            var Q82;
            Q82=sQuery(id+"F15.wireOp",EDGE,"E22.15.0.2");
            var Q83;
            Q83=sQuery(id+"F15.wireOp",EDGE,"E22.11.0.2");
            var Q84;
            Q84=sQuery(id+"F15.wireOp",EDGE,"E22.31.0.2");
            var Q85;
            Q85=sQuery(id+"F15.wireOp",EDGE,"E22.27.0.2");
            var Q86;
            Q86=sQuery(id+"F15.wireOp",EDGE,"E22.8.0.0");
            var Q87;
            Q87=sQuery(id+"F15.wireOp",EDGE,"E22.4.0.0");
            var Q88;
            Q88=sQuery(id+"F15.wireOp",EDGE,"E22.24.0.0");
            var Q89;
            Q89=sQuery(id+"F15.wireOp",EDGE,"E22.20.0.0");
            var Q90;
            Q90=sQuery(id+"F15.wireOp",EDGE,"E22.16.0.0");
            var Q91;
            Q91=sQuery(id+"F15.wireOp",EDGE,"E22.12.0.0");
            var Q92;
            Q92=sQuery(id+"F15.wireOp",EDGE,"E22.32.0.0");
            var Q93;
            Q93=sQuery(id+"F15.wireOp",EDGE,"E22.28.0.0");
            var Q94;
            Q94=sQuery(id+"F15.wireOp",EDGE,"E22.8.0.2");
            var Q95;
            Q95=sQuery(id+"F15.wireOp",EDGE,"E22.4.0.2");
            var Q96;
            Q96=sQuery(id+"F15.wireOp",EDGE,"E22.24.0.2");
            var Q97;
            Q97=sQuery(id+"F15.wireOp",EDGE,"E22.20.0.2");
            var Q98;
            Q98=sQuery(id+"F15.wireOp",EDGE,"E22.16.0.2");
            var Q99;
            Q99=sQuery(id+"F15.wireOp",EDGE,"E22.32.0.2");
            var Q100;
            Q100=sQuery(id+"F15.wireOp",EDGE,"E22.28.0.2");
            var Q101;
            Q101=sQuery(id+"F15.wireOp",EDGE,"E22.9.0.0");
            var Q102;
            Q102=sQuery(id+"F15.wireOp",EDGE,"E22.5.0.0");
            var Q103;
            Q103=sQuery(id+"F15.wireOp",EDGE,"E22.29.0.0");
            var Q104;
            Q104=sQuery(id+"F15.wireOp",EDGE,"E22.29.0.2");
            var Q105;
            Q105=sQuery(id+"F15.wireOp",EDGE,"E22.25.0.2");
            var Q106;
            Q106=sQuery(id+"F15.wireOp",EDGE,"E22.21.0.2");
            var Q107;
            Q107=sQuery(id+"F15.wireOp",EDGE,"E22.17.0.2");
            var Q108;
            Q108=sQuery(id+"F15.wireOp",EDGE,"E22.13.0.2");
            var Q109;
            Q109=sQuery(id+"F15.wireOp",EDGE,"E22.9.0.2");
            var Q110;
            Q110=sQuery(id+"F15.wireOp",EDGE,"E22.5.0.2");
            var Q111;
            Q111=sQuery(id+"F15.wireOp",EDGE,"E22.18.0.0");
            var Q112;
            Q112=sQuery(id+"F15.wireOp",EDGE,"E22.14.0.0");
            var Q113;
            Q113=sQuery(id+"F15.wireOp",EDGE,"E22.10.0.0");
            var Q114;
            Q114=sQuery(id+"F15.wireOp",EDGE,"E22.6.0.0");
            var Q115;
            Q115=sQuery(id+"F15.wireOp",EDGE,"E22.30.0.0");
            var Q116;
            Q116=sQuery(id+"F15.wireOp",EDGE,"E22.26.0.0");
            var Q117;
            Q117=sQuery(id+"F15.wireOp",EDGE,"E22.22.0.0");
            var Q118;
            Q118=sQuery(id+"F15.wireOp",EDGE,"E22.22.0.2");
            var Q119;
            Q119=sQuery(id+"F15.wireOp",EDGE,"E22.3.0.0");
            var Q120;
            Q120=sQuery(id+"F15.wireOp",EDGE,"E22.2.0.2");
            var Q121;
            Q121=sQuery(id+"F15.wireOp",EDGE,"E22.7.0.0");
            var Q122;
            Q122=sQuery(id+"F15.wireOp",EDGE,"E22.23.0.0");
            var Q123;
            Q123=sQuery(id+"F15.wireOp",EDGE,"E22.15.0.0");
            var Q124;
            Q124=sQuery(id+"F15.wireOp",EDGE,"E22.11.0.0");
            var Q125;
            Q125=sQuery(id+"F15.wireOp",EDGE,"E22.31.0.0");
            var Q126;
            Q126=sQuery(id+"F15.wireOp",EDGE,"E22.27.0.0");
            var Q127;
            Q127=sQuery(id+"F15.wireOp",EDGE,"E22.12.0.2");
            var Q128;
            Q128=sQuery(id+"F15.wireOp",EDGE,"E22.25.0.0");
            var Q129;
            Q129=sQuery(id+"F15.wireOp",EDGE,"E22.21.0.0");
            var Q130;
            Q130=sQuery(id+"F15.wireOp",EDGE,"E22.17.0.0");
            var Q131;
            Q131=sQuery(id+"F15.wireOp",EDGE,"E22.13.0.0");
            var Q132;
            Q132=sQuery(id+"F15.wireOp",EDGE,"E22.33.0.0");
            var Q133;
            Q133=sQuery(id+"F15.wireOp",EDGE,"E22.33.0.1");
            var Q134;
            Q134=sQuery(id+"F15.wireOp",EDGE,"E17");
            var Q135;
            Q135=sQuery(id+"F15.wireOp",EDGE,"E23");
            extrude(context, id + "F16", {"bodyType" : ToolBodyType.SURFACE, "surfaceEntities" : qUnion([Q0, Q1, Q2, Q3, Q4, Q5, Q6, Q7, Q8, Q9, Q10, Q11, Q12, Q13, Q14, Q15, Q16, Q17, Q18, Q19, Q20, Q21, Q22, Q23, Q24, Q25, Q26, Q27, Q28, Q29, Q30, Q31, Q32, Q33, Q34, Q35, Q36, Q37, Q38, Q39, Q40, Q41, Q42, Q43, Q44, Q45, Q46, Q47, Q48, Q49, Q50, Q51, Q52, Q53, Q54, Q55, Q56, Q57, Q58, Q59, Q60, Q61, Q62, Q63, Q64, Q65, Q66, Q67, Q68, Q69, Q70, Q71, Q72, Q73, Q74, Q75, Q76, Q77, Q78, Q79, Q80, Q81, Q82, Q83, Q84, Q85, Q86, Q87, Q88, Q89, Q90, Q91, Q92, Q93, Q94, Q95, Q96, Q97, Q98, Q99, Q100, Q101, Q102, Q103, Q104, Q105, Q106, Q107, Q108, Q109, Q110, Q111, Q112, Q113, Q114, Q115, Q116, Q117, Q118, Q119, Q120, Q121, Q122, Q123, Q124, Q125, Q126, Q127, Q128, Q129, Q130, Q131, Q132, Q133, Q134, Q135]), "oppositeDirection" : true, "depth" : 200 * mm});
        }
    });
